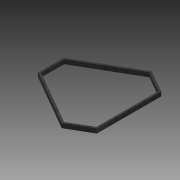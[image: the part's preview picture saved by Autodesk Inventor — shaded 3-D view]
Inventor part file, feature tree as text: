
AUTODESK INVENTOR PART (.ipt)
format: ipt  version: 2015 (Build 190159000, 159)  size: 88,576 bytes
history: native  units: in
note: dims shown in document units (in); Inventor stores cm internally (conversion verified against a paired STEP export)
features: extrude x1, sketch x1
ambient origin geometry x8: Origin, YZ Plane, XZ Plane, XY Plane, X Axis, Y Axis, Z Axis, Center Point
bodies: Body1 (feature_tree)
feature tree (2):
  extrude  "Extrusion6"  [1 undecoded]
  sketch  "Sketch1"  dims[d45=2.0in d46=0.0in]
note: 1 required parameter value undecoded (feature->parameter linkage not recoverable at this tier; creation-order binding heuristic only, values carry confidence <= 0.55)
